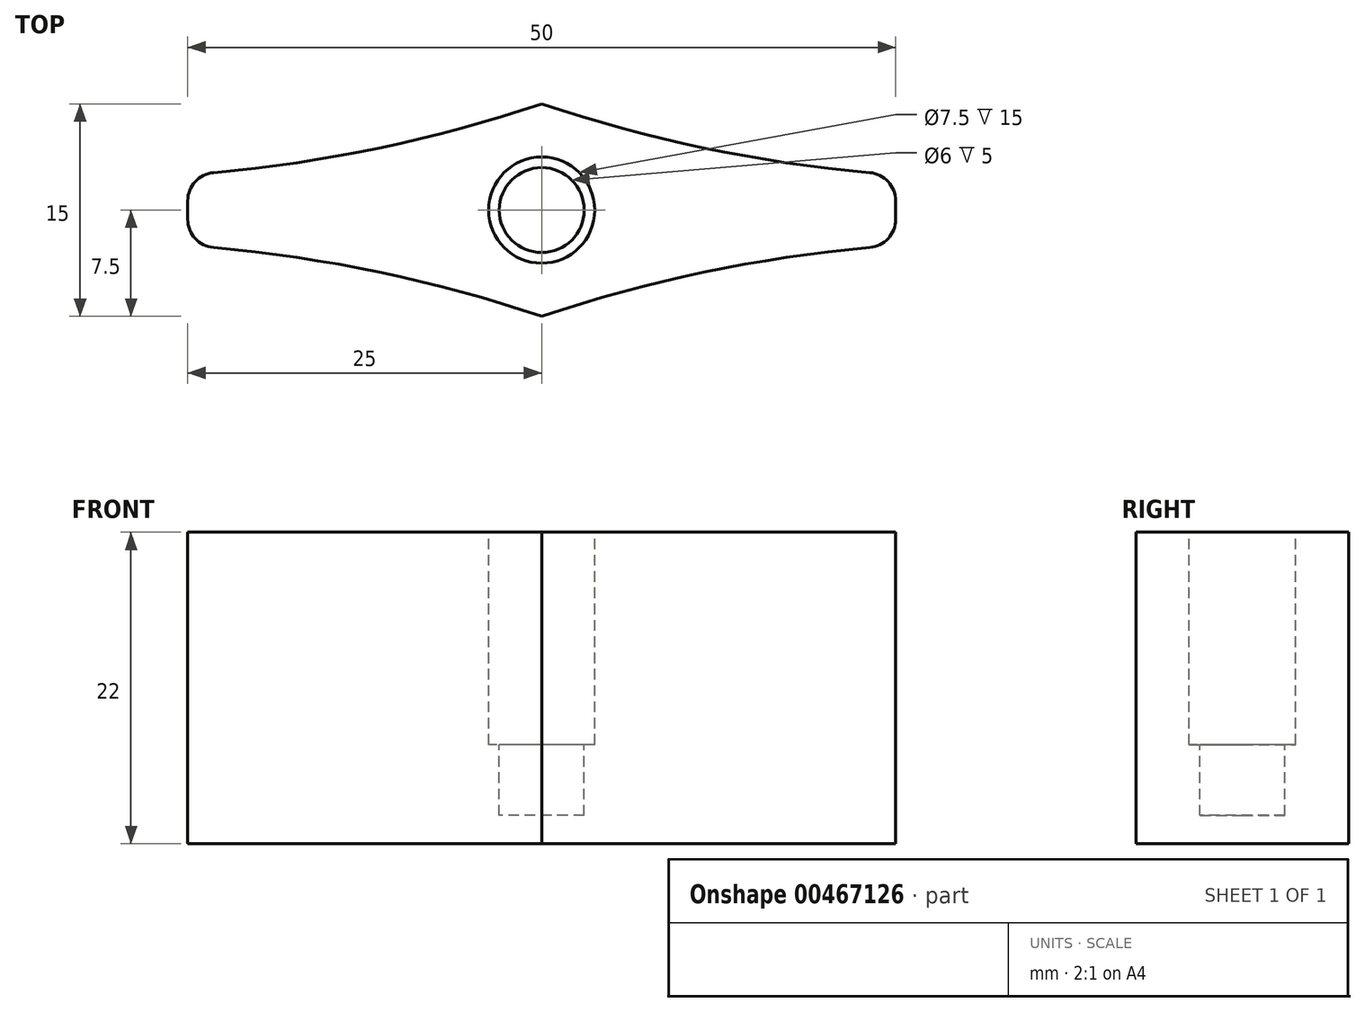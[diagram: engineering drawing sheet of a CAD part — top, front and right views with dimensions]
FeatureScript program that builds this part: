
annotation { "Feature Type Name" : "Feature", "Feature Type Description" : "" }
export const myFeature = defineFeature(function(context is Context, id is Id, definition is map)
    precondition{}
    {
        {
            var Q0;
            Q0=qCreatedBy(makeId("Top.planeOp"),FACE);
            var sketch = newSketch(context, id + "F0", { "sketchPlane" : qUnion([Q0])});
            skLineSegment(sketch, "E0.bottom", {"start": v(20, -7.5) * mm, "end": v(-20, -7.5) * mm});
            skLineSegment(sketch, "E0.top", {"start": v(20, 7.5) * mm, "end": v(-20, 7.5) * mm});
            skLineSegment(sketch, "E0.left", {"start": v(25, -0.65) * mm, "end": v(25, 0.65) * mm});
            skLineSegment(sketch, "E0.right", {"start": v(-25, -0.65) * mm, "end": v(-25, 0.65) * mm});
            skPoint(sketch, "E0.middle", {"position": v(0, 0) * mm});
            skCircle(sketch, "E1", {"center": v(0, 0) * mm, "radius": 3.75 * mm});
            skPoint(sketch, "E2.visualSharp", {"position": v(-25, 7.5) * mm});
            skArc(sketch, "E2.filletArc", {"start": v(-20, 7.5) * mm, "mid": v(-23.54, 6.04) * mm, "end": v(-25, 2.5) * mm});
            skPoint(sketch, "E3.visualSharp", {"position": v(-25, -7.5) * mm});
            skArc(sketch, "E3.filletArc", {"start": v(-25, -2.5) * mm, "mid": v(-23.54, -6.04) * mm, "end": v(-20, -7.5) * mm});
            skPoint(sketch, "E4.visualSharp", {"position": v(25, -7.5) * mm});
            skArc(sketch, "E4.filletArc", {"start": v(20, -7.5) * mm, "mid": v(23.54, -6.04) * mm, "end": v(25, -2.5) * mm});
            skPoint(sketch, "E5.visualSharp", {"position": v(25, 7.5) * mm});
            skArc(sketch, "E5.filletArc", {"start": v(25, 2.5) * mm, "mid": v(23.54, 6.04) * mm, "end": v(20, 7.5) * mm});
            skArc(sketch, "E6", {"start": v(-23.18, 2.65) * mm, "mid": v(-11.45, 4.4) * mm, "end": v(0, 7.5) * mm});
            skArc(sketch, "E7", {"start": v(0, -7.5) * mm, "mid": v(-11.45, -4.4) * mm, "end": v(-23.18, -2.65) * mm});
            skArc(sketch, "E8", {"start": v(0, 7.5) * mm, "mid": v(11.45, 4.4) * mm, "end": v(23.18, 2.65) * mm});
            skArc(sketch, "E9", {"start": v(23.18, -2.65) * mm, "mid": v(11.45, -4.4) * mm, "end": v(0, -7.5) * mm});
            skPoint(sketch, "E10.visualSharp", {"position": v(-25, 2.5) * mm});
            skArc(sketch, "E10.filletArc", {"start": v(-23.18, 2.65) * mm, "mid": v(-24.48, 2) * mm, "end": v(-25, 0.65) * mm});
            skPoint(sketch, "E11.visualSharp", {"position": v(-25, -2.5) * mm});
            skArc(sketch, "E11.filletArc", {"start": v(-25, -0.65) * mm, "mid": v(-24.48, -2) * mm, "end": v(-23.18, -2.65) * mm});
            skPoint(sketch, "E12.visualSharp", {"position": v(25, 2.5) * mm});
            skArc(sketch, "E12.filletArc", {"start": v(25, 0.65) * mm, "mid": v(24.48, 2) * mm, "end": v(23.18, 2.65) * mm});
            skPoint(sketch, "E13.visualSharp", {"position": v(25, -2.5) * mm});
            skArc(sketch, "E13.filletArc", {"start": v(23.18, -2.65) * mm, "mid": v(24.48, -2) * mm, "end": v(25, -0.65) * mm});
            skCircle(sketch, "E14", {"center": v(0, 0) * mm, "radius": 3 * mm});
            skSolve(sketch);
        }
        {
            var Q0;
            Q0 = qSketchRegion(id + "F0", true);
            var Q1;
            Q1=makeQuery(id+"F0.imprint","IMPRINT",FACE,{"disambiguationData":[TD([[makeQuery(id+"F0.imprint","IMPRINT",EDGE,{"derivedFrom":sQuery(id+"F0.wireOp",EDGE,"E1")}),1.0]])]});
            var Q2;
            Q2=makeQuery(id+"F0.imprint","IMPRINT",FACE,{"disambiguationData":[TD([[makeQuery(id+"F0.imprint","IMPRINT",EDGE,{"derivedFrom":sQuery(id+"F0.wireOp",EDGE,"E14")}),1.0]])]});
            extrude(context, id + "F1", {"entities" : qUnion([Q0, Q1, Q2]), "depth" : 22 * mm});
        }
        {
            var Q0;
            Q0=makeQuery(id+"F1.opExtrude","CAP_FACE",FACE,{"disambiguationData":[OSD([sQuery(id+"F0.wireOp",EDGE,"E0.left"),sQuery(id+"F0.wireOp",EDGE,"E0.right"),sQuery(id+"F0.wireOp",EDGE,"E6"),sQuery(id+"F0.wireOp",EDGE,"E7"),sQuery(id+"F0.wireOp",EDGE,"E8"),sQuery(id+"F0.wireOp",EDGE,"E9"),sQuery(id+"F0.wireOp",EDGE,"E10.filletArc"),sQuery(id+"F0.wireOp",EDGE,"E11.filletArc"),sQuery(id+"F0.wireOp",EDGE,"E12.filletArc"),sQuery(id+"F0.wireOp",EDGE,"E13.filletArc")])],"isStart":false});
            var sketch = newSketch(context, id + "F2", { "sketchPlane" : qUnion([Q0])});
            skCircle(sketch, "E15", {"center": v(0, 0) * mm, "radius": 3 * mm});
            skCircle(sketch, "E16", {"center": v(0, 0) * mm, "radius": 3.75 * mm});
            skSolve(sketch);
        }
        {
            var Q0;
            Q0=makeQuery(id+"F2.imprint","IMPRINT",FACE,{"disambiguationData":[TD([[makeQuery(id+"F2.imprint","IMPRINT",EDGE,{"derivedFrom":sQuery(id+"F2.wireOp",EDGE,"E15")}),1.0]])]});
            extrude(context, id + "F3", {"entities" : qUnion([Q0]), "operationType" : NewBodyOperationType.REMOVE, "oppositeDirection" : true, "depth" : 20 * mm});
        }
        {
            var Q0;
            Q0=makeQuery(id+"F2.imprint","IMPRINT",FACE,{"disambiguationData":[TD([[makeQuery(id+"F2.imprint","IMPRINT",EDGE,{"derivedFrom":sQuery(id+"F2.wireOp",EDGE,"E15")}),-1.0]])]});
            extrude(context, id + "F4", {"entities" : qUnion([Q0]), "operationType" : NewBodyOperationType.REMOVE, "oppositeDirection" : true, "depth" : 15 * mm});
        }
    });
